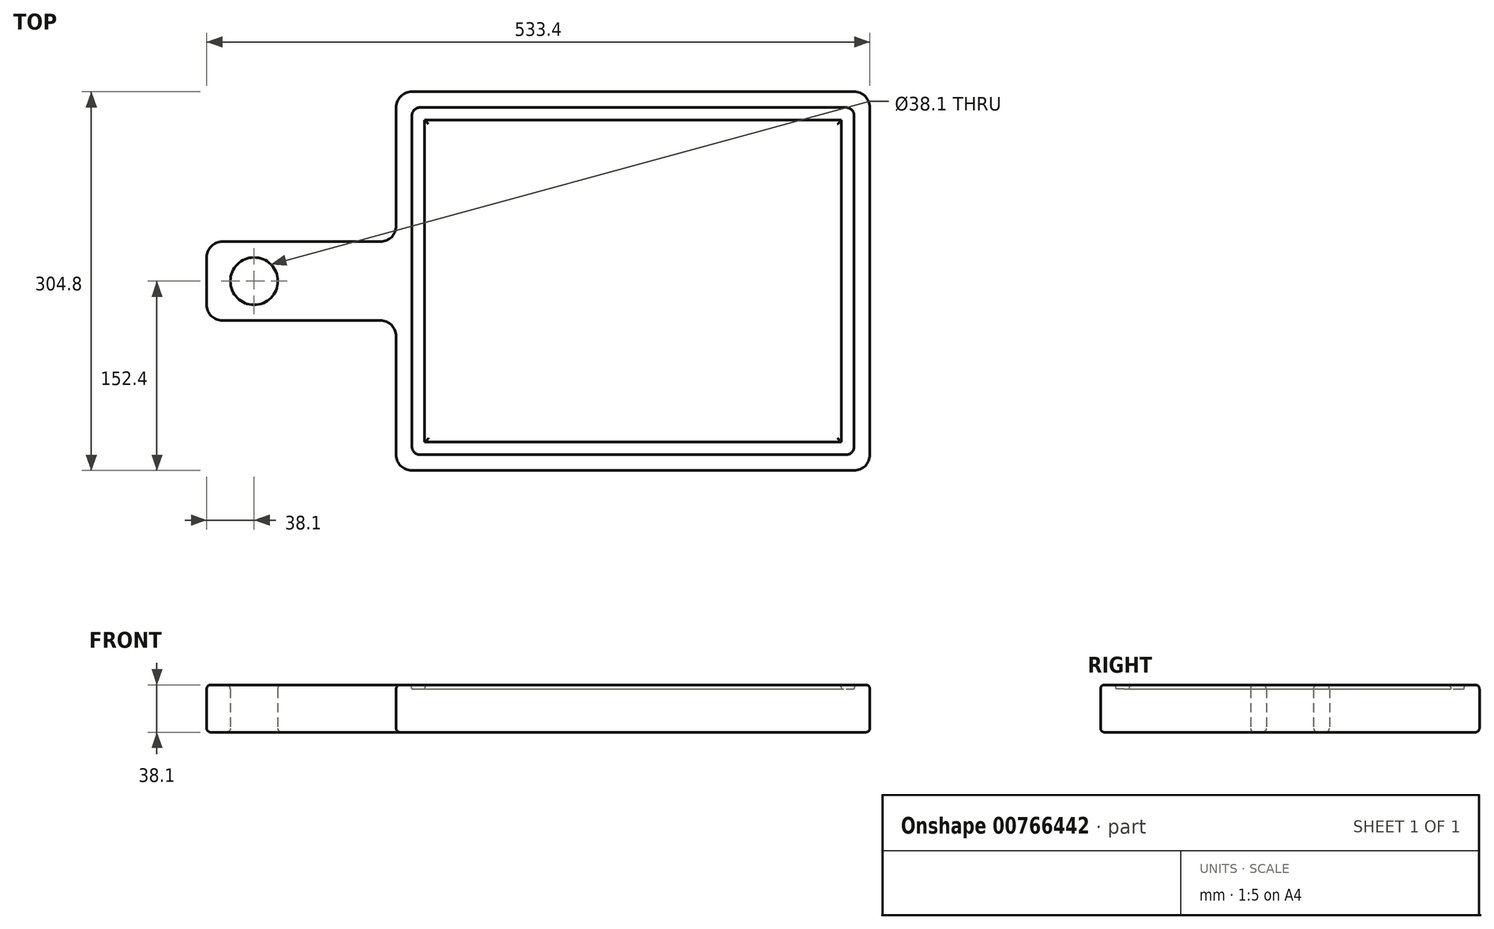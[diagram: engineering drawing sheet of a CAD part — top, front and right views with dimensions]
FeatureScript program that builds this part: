
annotation { "Feature Type Name" : "Feature", "Feature Type Description" : "" }
export const myFeature = defineFeature(function(context is Context, id is Id, definition is map)
    precondition{}
    {
        {
            var Q0;
            Q0=qCreatedBy(makeId("Top.planeOp"),FACE);
            var sketch = newSketch(context, id + "F0", { "sketchPlane" : qUnion([Q0])});
            skLineSegment(sketch, "E0.bottom", {"start": v(0, 0) * mm, "end": v(381, 0) * mm});
            skLineSegment(sketch, "E0.top", {"start": v(0, 304.8) * mm, "end": v(381, 304.8) * mm});
            skLineSegment(sketch, "E0.left", {"start": v(0, 0) * mm, "end": v(0, 304.8) * mm});
            skLineSegment(sketch, "E0.right", {"start": v(381, 0) * mm, "end": v(381, 304.8) * mm});
            skLineSegment(sketch, "E1.bottom", {"start": v(0, 184.15) * mm, "end": v(-152.4, 184.15) * mm});
            skLineSegment(sketch, "E1.top", {"start": v(0, 120.65) * mm, "end": v(-152.4, 120.65) * mm});
            skLineSegment(sketch, "E1.left", {"start": v(0, 184.15) * mm, "end": v(0, 120.65) * mm});
            skLineSegment(sketch, "E1.right", {"start": v(-152.4, 184.15) * mm, "end": v(-152.4, 120.65) * mm});
            skSolve(sketch);
        }
        {
            var Q0;
            Q0=makeQuery(id+"F0.imprint","IMPRINT",FACE,{"disambiguationData":[TD([[makeQuery(id+"F0.imprint","IMPRINT",EDGE,{"derivedFrom":sQuery(id+"F0.wireOp",EDGE,"E1.bottom")}),1.0]])]});
            var Q1;
            {var subQ3=sQuery(id+"F0.wireOp",EDGE,"E0.bottom");Q1=makeQuery(id+"F0.imprint","IMPRINT",FACE,{"disambiguationData":[TD([[makeQuery(id+"F0.imprint","IMPRINT",EDGE,{"derivedFrom":subQ3}),1.0]])]});}
            extrude(context, id + "F1", {"entities" : qUnion([Q0, Q1]), "depth" : 38.1 * mm, "offsetDistance" : 25.4 * mm});
        }
        {
            var Q0;
            Q0=makeQuery(id+"F1.opExtrude","CAP_FACE",FACE,{"disambiguationData":[OSD([sQuery(id+"F0.wireOp",EDGE,"E0.bottom"),sQuery(id+"F0.wireOp",EDGE,"E0.top"),sQuery(id+"F0.wireOp",EDGE,"E0.left"),sQuery(id+"F0.wireOp",EDGE,"E0.right"),sQuery(id+"F0.wireOp",EDGE,"E1.bottom"),sQuery(id+"F0.wireOp",EDGE,"E1.top"),sQuery(id+"F0.wireOp",EDGE,"E1.right")])],"isStart":true});
            var sketch = newSketch(context, id + "F2", { "sketchPlane" : qUnion([Q0])});
            skCircle(sketch, "E2", {"center": v(-114.3, -152.4) * mm, "radius": 19.05 * mm});
            skSolve(sketch);
        }
        {
            var Q0;
            Q0 = qSketchRegion(id + "F2", true);
            extrude(context, id + "F3", {"entities" : qUnion([Q0]), "operationType" : NewBodyOperationType.REMOVE, "oppositeDirection" : true, "depth" : 38.1 * mm, "offsetDistance" : 25.4 * mm});
        }
        {
            var Q0;
            Q0=makeQuery(id+"F1.opExtrude","CAP_FACE",FACE,{"disambiguationData":[OSD([sQuery(id+"F0.wireOp",EDGE,"E0.bottom"),sQuery(id+"F0.wireOp",EDGE,"E0.top"),sQuery(id+"F0.wireOp",EDGE,"E0.left"),sQuery(id+"F0.wireOp",EDGE,"E0.right"),sQuery(id+"F0.wireOp",EDGE,"E1.bottom"),sQuery(id+"F0.wireOp",EDGE,"E1.top"),sQuery(id+"F0.wireOp",EDGE,"E1.right")])],"isStart":false});
            var sketch = newSketch(context, id + "F4", { "sketchPlane" : qUnion([Q0])});
            skLineSegment(sketch, "E3.0", {"start": v(12.7, 12.7) * mm, "end": v(12.7, 120.65) * mm});
            skLineSegment(sketch, "E3.1", {"start": v(12.7, 184.15) * mm, "end": v(12.7, 292.1) * mm});
            skLineSegment(sketch, "E3.2", {"start": v(12.7, 292.1) * mm, "end": v(368.3, 292.1) * mm});
            skLineSegment(sketch, "E3.3", {"start": v(368.3, 12.7) * mm, "end": v(368.3, 292.1) * mm});
            skLineSegment(sketch, "E3.4", {"start": v(12.7, 12.7) * mm, "end": v(368.3, 12.7) * mm});
            skLineSegment(sketch, "E4", {"start": v(12.7, 184.15) * mm, "end": v(12.7, 120.65) * mm});
            skLineSegment(sketch, "E5.0", {"start": v(22.86, 184.15) * mm, "end": v(22.86, 281.94) * mm});
            skLineSegment(sketch, "E5.1", {"start": v(358.14, 22.86) * mm, "end": v(358.14, 281.94) * mm});
            skLineSegment(sketch, "E5.2", {"start": v(22.86, 22.86) * mm, "end": v(358.14, 22.86) * mm});
            skLineSegment(sketch, "E5.3", {"start": v(22.86, 281.94) * mm, "end": v(358.14, 281.94) * mm});
            skLineSegment(sketch, "E5.4", {"start": v(22.86, 22.86) * mm, "end": v(22.86, 120.65) * mm});
            skLineSegment(sketch, "E5.5", {"start": v(22.86, 184.15) * mm, "end": v(22.86, 120.65) * mm});
            skSolve(sketch);
        }
        {
            var Q0;
            Q0=makeQuery(id+"F4.imprint","IMPRINT",FACE,{"disambiguationData":[TD([[makeQuery(id+"F4.imprint","IMPRINT",EDGE,{"derivedFrom":sQuery(id+"F4.wireOp",EDGE,"E3.0")}),-1.0]])]});
            extrude(context, id + "F5", {"entities" : qUnion([Q0]), "operationType" : NewBodyOperationType.REMOVE, "oppositeDirection" : true, "depth" : 3.17 * mm, "offsetDistance" : 25.4 * mm});
        }
        {
            var Q0;
            Q0=makeQuery(id+"F5.boolean.opBoolean","COPY",EDGE,{"derivedFrom":makeQuery(id+"F5.opExtrude","SWEPT_EDGE",EDGE,{"disambiguationData":[OSD([sQuery(id+"F4.wireOp",EDGE,"E3.1"),sQuery(id+"F4.wireOp",EDGE,"E3.2")])]})});
            var Q1;
            Q1=makeQuery(id+"F5.boolean.opBoolean","COPY",EDGE,{"derivedFrom":makeQuery(id+"F5.opExtrude","SWEPT_EDGE",EDGE,{"disambiguationData":[OSD([sQuery(id+"F4.wireOp",EDGE,"E3.2"),sQuery(id+"F4.wireOp",EDGE,"E3.3")])]})});
            var Q2;
            Q2=makeQuery(id+"F5.boolean.opBoolean","COPY",EDGE,{"derivedFrom":makeQuery(id+"F5.opExtrude","SWEPT_EDGE",EDGE,{"disambiguationData":[OSD([sQuery(id+"F4.wireOp",EDGE,"E3.3"),sQuery(id+"F4.wireOp",EDGE,"E3.4")])]})});
            var Q3;
            Q3=makeQuery(id+"F5.boolean.opBoolean","COPY",EDGE,{"derivedFrom":makeQuery(id+"F5.opExtrude","SWEPT_EDGE",EDGE,{"disambiguationData":[OSD([sQuery(id+"F4.wireOp",EDGE,"E3.0"),sQuery(id+"F4.wireOp",EDGE,"E3.4")])]})});
            fillet(context, id + "F6", {"entities" : qUnion([Q0, Q1, Q2, Q3]), "radius" : 6.35 * mm, "tangentPropagation" : true, "allowEdgeOverflow" : false});
        }
        {
            var Q0;
            Q0=makeQuery(id+"F1.opExtrude","SWEPT_EDGE",EDGE,{"disambiguationData":[OSD([sQuery(id+"F0.wireOp",EDGE,"E0.bottom"),sQuery(id+"F0.wireOp",EDGE,"E0.left")])]});
            var Q1;
            Q1=makeQuery(id+"F1.opExtrude","SWEPT_EDGE",EDGE,{"disambiguationData":[OSD([sQuery(id+"F0.wireOp",EDGE,"E1.top"),sQuery(id+"F0.wireOp",EDGE,"E1.right")])]});
            var Q2;
            Q2=makeQuery(id+"F1.opExtrude","SWEPT_EDGE",EDGE,{"disambiguationData":[OSD([sQuery(id+"F0.wireOp",EDGE,"E1.bottom"),sQuery(id+"F0.wireOp",EDGE,"E1.right")])]});
            var Q3;
            Q3=makeQuery(id+"F1.opExtrude","SWEPT_EDGE",EDGE,{"disambiguationData":[OSD([sQuery(id+"F0.wireOp",EDGE,"E0.top"),sQuery(id+"F0.wireOp",EDGE,"E0.left")])]});
            var Q4;
            Q4=makeQuery(id+"F1.opExtrude","SWEPT_EDGE",EDGE,{"disambiguationData":[OSD([sQuery(id+"F0.wireOp",EDGE,"E0.top"),sQuery(id+"F0.wireOp",EDGE,"E0.right")])]});
            var Q5;
            Q5=makeQuery(id+"F1.opExtrude","SWEPT_EDGE",EDGE,{"disambiguationData":[OSD([sQuery(id+"F0.wireOp",EDGE,"E0.bottom"),sQuery(id+"F0.wireOp",EDGE,"E0.right")])]});
            var Q6;
            Q6=makeQuery(id+"F1.opExtrude","SWEPT_EDGE",EDGE,{"disambiguationData":[OSD([sQuery(id+"F0.wireOp",EDGE,"E0.left"),sQuery(id+"F0.wireOp",EDGE,"E1.bottom"),sQuery(id+"F0.wireOp",EDGE,"E1.left")])]});
            var Q7;
            Q7=makeQuery(id+"F1.opExtrude","SWEPT_EDGE",EDGE,{"disambiguationData":[OSD([sQuery(id+"F0.wireOp",EDGE,"E0.left"),sQuery(id+"F0.wireOp",EDGE,"E1.top"),sQuery(id+"F0.wireOp",EDGE,"E1.left")])]});
            fillet(context, id + "F7", {"entities" : qUnion([Q0, Q1, Q2, Q3, Q4, Q5, Q6, Q7]), "radius" : 12.7 * mm, "tangentPropagation" : true, "allowEdgeOverflow" : false});
        }
        {
            var Q0;
            Q0=makeQuery(id+"F5.boolean.opBoolean","SPLIT",FACE,{"disambiguationData":[TD([makeQuery(id+"F5.opExtrude","SWEPT_FACE",FACE,{"disambiguationData":[OSD([sQuery(id+"F4.wireOp",EDGE,"E5.1")])]})])],"derivedFrom":makeQuery(id+"F1.opExtrude","CAP_FACE",FACE,{"disambiguationData":[OSD([sQuery(id+"F0.wireOp",EDGE,"E0.bottom"),sQuery(id+"F0.wireOp",EDGE,"E0.top"),sQuery(id+"F0.wireOp",EDGE,"E0.left"),sQuery(id+"F0.wireOp",EDGE,"E0.right"),sQuery(id+"F0.wireOp",EDGE,"E1.bottom"),sQuery(id+"F0.wireOp",EDGE,"E1.top"),sQuery(id+"F0.wireOp",EDGE,"E1.right")])],"isStart":false})});
            var Q1;
            {var subQ0=sQuery(id+"F0.wireOp",EDGE,"E0.left");var subQ1=sQuery(id+"F0.wireOp",EDGE,"E0.top");var subQ3=sQuery(id+"F0.wireOp",EDGE,"E1.bottom");var subQ4=sQuery(id+"F0.wireOp",EDGE,"E1.right");var subQ5=sQuery(id+"F0.wireOp",EDGE,"E1.top");var subQ6=sQuery(id+"F0.wireOp",EDGE,"E0.right");var subQ7=sQuery(id+"F0.wireOp",EDGE,"E0.bottom");Q1=makeQuery(id+"F5.boolean.opBoolean","SPLIT",FACE,{"disambiguationData":[TD([makeQuery(id+"F1.opExtrude","SWEPT_FACE",FACE,{"disambiguationData":[OSD([subQ7])]})])],"derivedFrom":makeQuery(id+"F1.opExtrude","CAP_FACE",FACE,{"disambiguationData":[OSD([subQ7,subQ1,subQ0,subQ6,subQ3,subQ5,subQ4])],"isStart":false})});}
            var Q2;
            Q2=makeQuery(id+"F1.opExtrude","CAP_FACE",FACE,{"disambiguationData":[OSD([sQuery(id+"F0.wireOp",EDGE,"E0.bottom"),sQuery(id+"F0.wireOp",EDGE,"E0.top"),sQuery(id+"F0.wireOp",EDGE,"E0.left"),sQuery(id+"F0.wireOp",EDGE,"E0.right"),sQuery(id+"F0.wireOp",EDGE,"E1.bottom"),sQuery(id+"F0.wireOp",EDGE,"E1.top"),sQuery(id+"F0.wireOp",EDGE,"E1.right")])],"isStart":true});
            fillet(context, id + "F8", {"entities" : qUnion([Q0, Q1, Q2]), "radius" : 3.17 * mm, "tangentPropagation" : true, "allowEdgeOverflow" : false});
        }
    });
